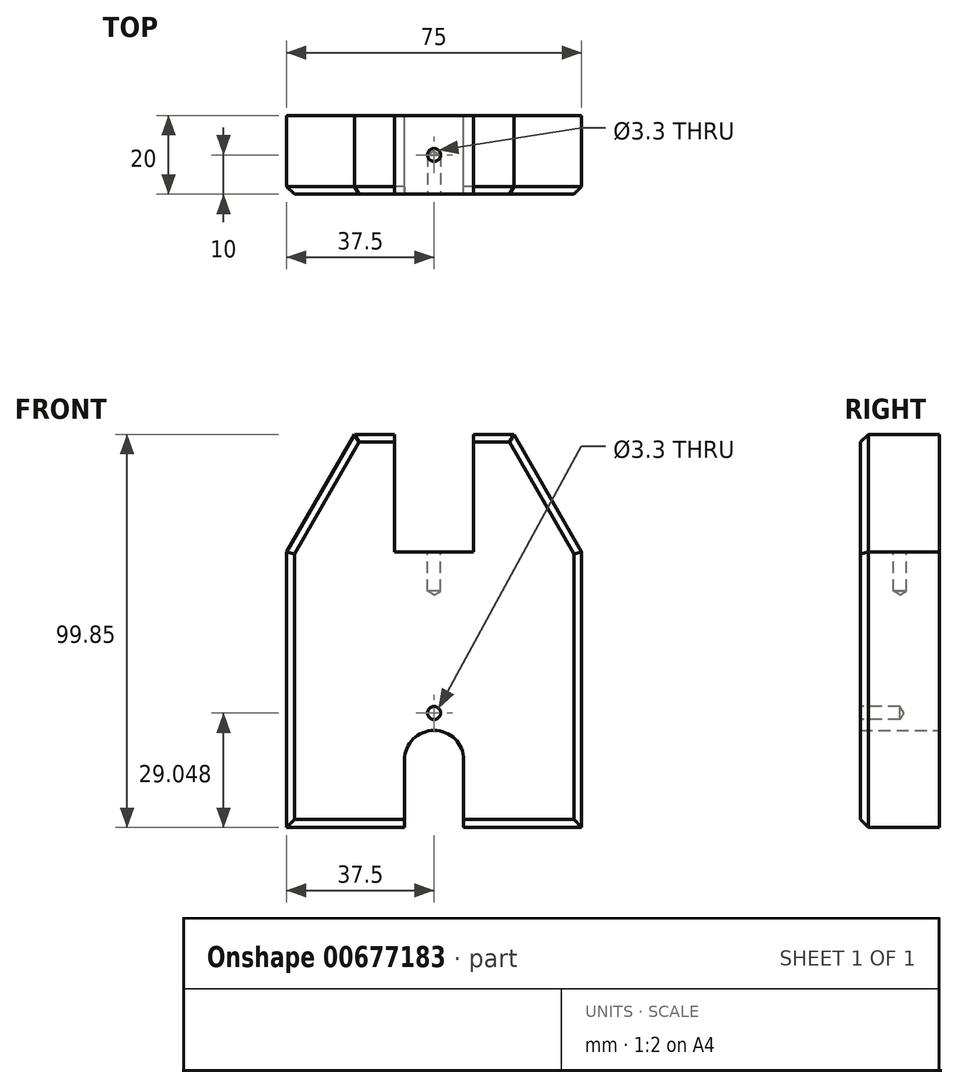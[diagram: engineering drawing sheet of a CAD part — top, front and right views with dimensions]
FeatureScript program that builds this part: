
annotation { "Feature Type Name" : "Feature", "Feature Type Description" : "" }
export const myFeature = defineFeature(function(context is Context, id is Id, definition is map)
    precondition{}
    {
        {
            var Q0;
            Q0=qCreatedBy(makeId("Front.planeOp"),FACE);
            var sketch = newSketch(context, id + "F0", { "sketchPlane" : qUnion([Q0])});
            skLineSegment(sketch, "E0.bottom", {"start": v(37.5, -35) * mm, "end": v(-37.5, -35) * mm});
            skLineSegment(sketch, "E0.top", {"start": v(37.5, 35) * mm, "end": v(-37.5, 35) * mm});
            skLineSegment(sketch, "E0.left", {"start": v(37.5, -35) * mm, "end": v(37.5, 35) * mm});
            skLineSegment(sketch, "E0.right", {"start": v(-37.5, -35) * mm, "end": v(-37.5, 35) * mm});
            skPoint(sketch, "E0.middle", {"position": v(0, 0) * mm});
            skLineSegment(sketch, "E1", {"start": v(37.5, 35) * mm, "end": v(20.27, 64.85) * mm});
            skLineSegment(sketch, "E2", {"start": v(20.27, 64.85) * mm, "end": v(10, 64.85) * mm});
            skLineSegment(sketch, "E3", {"start": v(10, 64.85) * mm, "end": v(10, 35) * mm});
            skPoint(sketch, "E4.MirrorCS.start.orphan", {"position": v(20.27, 64.85) * mm});
            skLineSegment(sketch, "E5", {"start": v(-37.5, 35) * mm, "end": v(-20.27, 64.85) * mm});
            skLineSegment(sketch, "E6", {"start": v(-20.27, 64.85) * mm, "end": v(-10, 64.85) * mm});
            skLineSegment(sketch, "E7", {"start": v(-10, 64.85) * mm, "end": v(-10, 35) * mm});
            skLineSegment(sketch, "E8", {"start": v(-7.5, -35) * mm, "end": v(-7.5, -17.87) * mm});
            skLineSegment(sketch, "E9", {"start": v(7.5, -17.87) * mm, "end": v(7.5, -35) * mm});
            skArc(sketch, "E10", {"start": v(7.5, -17.87) * mm, "mid": v(0, -10.37) * mm, "end": v(-7.5, -17.87) * mm});
            skSolve(sketch);
        }
        {
            var Q0;
            Q0 = qSketchRegion(id + "F0", true);
            extrude(context, id + "F1", {"entities" : qUnion([Q0]), "endBound" : BoundingType.SYMMETRIC, "depth" : 20 * mm, "offsetDistance" : 25 * mm});
        }
        {
            var Q0;
            Q0=qCreatedBy(makeId("Front.planeOp"),FACE);
            var sketch = newSketch(context, id + "F2", { "sketchPlane" : qUnion([Q0])});
            skLineSegment(sketch, "E11.0", {"start": v(-7.5, -35) * mm, "end": v(-7.5, -17.87) * mm});
            skArc(sketch, "E12.0", {"start": v(7.5, -17.87) * mm, "mid": v(0, -10.37) * mm, "end": v(-7.5, -17.87) * mm});
            skLineSegment(sketch, "E13.0", {"start": v(7.5, -17.87) * mm, "end": v(7.5, -35) * mm});
            skLineSegment(sketch, "E14.0", {"start": v(7.5, -35) * mm, "end": v(-7.5, -35) * mm});
            skPoint(sketch, "E15.orphan", {"position": v(-37.5, -35) * mm});
            skPoint(sketch, "E16.orphan", {"position": v(37.5, -35) * mm});
            skSolve(sketch);
        }
        {
            var Q0;
            Q0 = qSketchRegion(id + "F2", true);
            extrude(context, id + "F3", {"entities" : qUnion([Q0]), "operationType" : NewBodyOperationType.REMOVE, "endBound" : BoundingType.SYMMETRIC, "depth" : 50 * mm, "offsetDistance" : 25 * mm});
        }
        {
            var Q0;
            Q0=makeQuery(id+"F1.opExtrude","CAP_EDGE",EDGE,{"disambiguationData":[OSD([sQuery(id+"F0.wireOp",EDGE,"E0.left")])],"isStart":false});
            var Q1;
            Q1=makeQuery(id+"F1.opExtrude","CAP_EDGE",EDGE,{"disambiguationData":[OSD([sQuery(id+"F0.wireOp",EDGE,"E1")])],"isStart":false});
            var Q2;
            {var subQ0=sQuery(id+"F0.wireOp",EDGE,"E0.bottom");var subQ1=sQuery(id+"F0.wireOp",EDGE,"E0.left");Q2=makeQuery(id+"F3.boolean.opBoolean","SPLIT",EDGE,{"disambiguationData":[TD([makeQuery(id+"F1.opExtrude","SWEPT_FACE",FACE,{"disambiguationData":[OSD([subQ1])]})])],"derivedFrom":makeQuery(id+"F1.opExtrude","CAP_EDGE",EDGE,{"disambiguationData":[OSD([subQ0])],"isStart":false})});}
            var Q3;
            {var subQ0=sQuery(id+"F0.wireOp",EDGE,"E0.bottom");var subQ1=sQuery(id+"F0.wireOp",EDGE,"E0.right");Q3=makeQuery(id+"F3.boolean.opBoolean","SPLIT",EDGE,{"disambiguationData":[TD([makeQuery(id+"F1.opExtrude","SWEPT_FACE",FACE,{"disambiguationData":[OSD([subQ1])]})])],"derivedFrom":makeQuery(id+"F1.opExtrude","CAP_EDGE",EDGE,{"disambiguationData":[OSD([subQ0])],"isStart":false})});}
            var Q4;
            Q4=makeQuery(id+"F1.opExtrude","CAP_EDGE",EDGE,{"disambiguationData":[OSD([sQuery(id+"F0.wireOp",EDGE,"E0.right")])],"isStart":false});
            var Q5;
            Q5=makeQuery(id+"F1.opExtrude","CAP_EDGE",EDGE,{"disambiguationData":[OSD([sQuery(id+"F0.wireOp",EDGE,"E5")])],"isStart":false});
            var Q6;
            Q6=makeQuery(id+"F1.opExtrude","CAP_EDGE",EDGE,{"disambiguationData":[OSD([sQuery(id+"F0.wireOp",EDGE,"E6")])],"isStart":false});
            var Q7;
            Q7=makeQuery(id+"F1.opExtrude","CAP_EDGE",EDGE,{"disambiguationData":[OSD([sQuery(id+"F0.wireOp",EDGE,"E2")])],"isStart":false});
            chamfer(context, id + "F4", {"entities" : qUnion([Q0, Q1, Q2, Q3, Q4, Q5, Q6, Q7]), "width" : 2 * mm, "tangentPropagation" : true});
        }
        {
            var Q0;
            Q0=makeQuery(id+"F1.opExtrude","CAP_FACE",FACE,{"disambiguationData":[OSD([sQuery(id+"F0.wireOp",EDGE,"E0.bottom"),sQuery(id+"F0.wireOp",EDGE,"E0.top"),sQuery(id+"F0.wireOp",EDGE,"E0.left"),sQuery(id+"F0.wireOp",EDGE,"E0.right"),sQuery(id+"F0.wireOp",EDGE,"E1"),sQuery(id+"F0.wireOp",EDGE,"E2"),sQuery(id+"F0.wireOp",EDGE,"E3"),sQuery(id+"F0.wireOp",EDGE,"E5"),sQuery(id+"F0.wireOp",EDGE,"E6"),sQuery(id+"F0.wireOp",EDGE,"E7")])],"isStart":false});
            var sketch = newSketch(context, id + "F5", { "sketchPlane" : qUnion([Q0])});
            skPoint(sketch, "E17", {"position": v(0, -5.95) * mm});
            skSolve(sketch);
        }
        {
            var Q0;
            Q0=sQuery(id+"F5.wireOp",VERTEX,"E17");
            var Q1;
            Q1=makeQuery(id+"F1.opExtrude","SWEPT_BODY",BODY,{"disambiguationData":[OSD([sQuery(id+"F0.wireOp",EDGE,"E0.bottom"),sQuery(id+"F0.wireOp",EDGE,"E0.top"),sQuery(id+"F0.wireOp",EDGE,"E0.left"),sQuery(id+"F0.wireOp",EDGE,"E0.right"),sQuery(id+"F0.wireOp",EDGE,"E1"),sQuery(id+"F0.wireOp",EDGE,"E2"),sQuery(id+"F0.wireOp",EDGE,"E3"),sQuery(id+"F0.wireOp",EDGE,"E5"),sQuery(id+"F0.wireOp",EDGE,"E6"),sQuery(id+"F0.wireOp",EDGE,"E7")])]});
            hole(context, id + "F6", {"style" : HoleStyle.SIMPLE, "endStyle" : HoleEndStyle.BLIND, "standardTappedOrClearance" : lookupTablePath({ "standard" : "ISO", "fit" : "Normal", "size" : "M3", "type" : "Clearance" }), "standardBlindInLast" : lookupTablePath({ "fit" : "Standard", "standard" : "ISO", "size" : "M3", "type" : "Clearance" }), "holeDiameter" : 3.3 * mm, "majorDiameter" : 4 * mm, "holeDepth" : 10 * mm, "isTappedThrough" : true, "tappedDepth" : 12 * mm, "tapClearance" : 3, "locations" : qUnion([Q0]), "scope" : qUnion([Q1])});
        }
        {
            var Q0;
            Q0=makeQuery(id+"F1.opExtrude","SWEPT_FACE",FACE,{"disambiguationData":[OSD([sQuery(id+"F0.wireOp",EDGE,"E0.top")])]});
            var sketch = newSketch(context, id + "F7", { "sketchPlane" : qUnion([Q0])});
            skPoint(sketch, "E18", {"position": v(0, 0) * mm});
            skSolve(sketch);
        }
        {
            var Q0;
            Q0=sQuery(id+"F7.wireOp",VERTEX,"E18");
            var Q1;
            Q1=makeQuery(id+"F1.opExtrude","SWEPT_BODY",BODY,{"disambiguationData":[OSD([sQuery(id+"F0.wireOp",EDGE,"E0.bottom"),sQuery(id+"F0.wireOp",EDGE,"E0.top"),sQuery(id+"F0.wireOp",EDGE,"E0.left"),sQuery(id+"F0.wireOp",EDGE,"E0.right"),sQuery(id+"F0.wireOp",EDGE,"E1"),sQuery(id+"F0.wireOp",EDGE,"E2"),sQuery(id+"F0.wireOp",EDGE,"E3"),sQuery(id+"F0.wireOp",EDGE,"E5"),sQuery(id+"F0.wireOp",EDGE,"E6"),sQuery(id+"F0.wireOp",EDGE,"E7")])]});
            hole(context, id + "F8", {"style" : HoleStyle.SIMPLE, "endStyle" : HoleEndStyle.BLIND, "standardTappedOrClearance" : lookupTablePath({ "standard" : "ISO", "fit" : "Normal", "size" : "M3", "type" : "Clearance" }), "standardBlindInLast" : lookupTablePath({ "fit" : "Standard", "standard" : "ISO", "size" : "M3", "type" : "Clearance" }), "holeDiameter" : 3.3 * mm, "majorDiameter" : 5 * mm, "holeDepth" : 10 * mm, "isTappedThrough" : true, "tappedDepth" : 12 * mm, "tapClearance" : 3, "locations" : qUnion([Q0]), "scope" : qUnion([Q1])});
        }
    });
